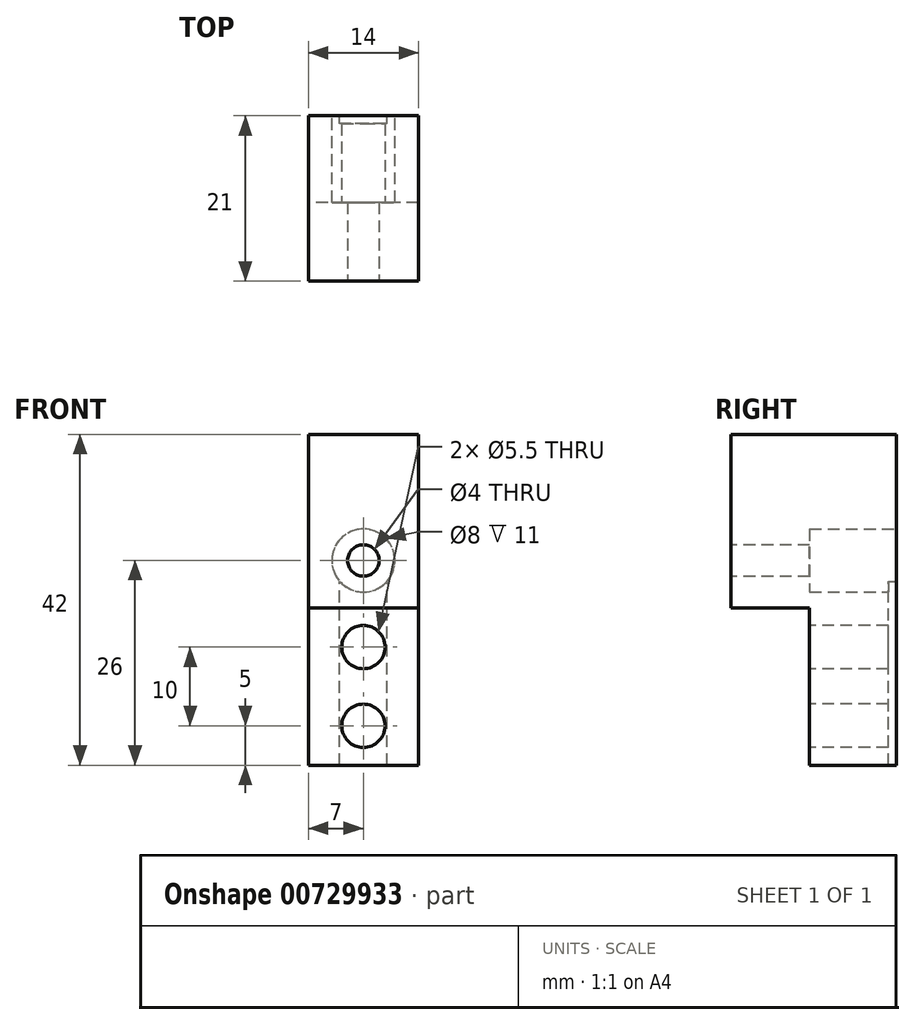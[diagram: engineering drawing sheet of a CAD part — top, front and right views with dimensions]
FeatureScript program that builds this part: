
annotation { "Feature Type Name" : "Feature", "Feature Type Description" : "" }
export const myFeature = defineFeature(function(context is Context, id is Id, definition is map)
    precondition{}
    {
        {
            var Q0;
            Q0=qCreatedBy(makeId("Front.planeOp"),FACE);
            var sketch = newSketch(context, id + "F0", { "sketchPlane" : qUnion([Q0])});
            skLineSegment(sketch, "E0.bottom", {"start": v(0, 0) * mm, "end": v(-14, 0) * mm});
            skLineSegment(sketch, "E0.top", {"start": v(0, 42) * mm, "end": v(-14, 42) * mm});
            skLineSegment(sketch, "E0.left", {"start": v(0, 0) * mm, "end": v(0, 42) * mm});
            skLineSegment(sketch, "E0.right", {"start": v(-14, 0) * mm, "end": v(-14, 42) * mm});
            skCircle(sketch, "E1", {"center": v(-7, 15) * mm, "radius": 2.75 * mm});
            skCircle(sketch, "E2", {"center": v(-7, 5) * mm, "radius": 2.75 * mm});
            skLineSegment(sketch, "E3", {"start": v(-14, 20) * mm, "end": v(0, 20) * mm});
            skCircle(sketch, "E4", {"center": v(-7, 26) * mm, "radius": 2 * mm});
            skSolve(sketch);
        }
        {
            var Q0;
            {var subQ1=sQuery(id+"F0.wireOp",EDGE,"E0.top");Q0=makeQuery(id+"F0.imprint","IMPRINT",FACE,{"disambiguationData":[TD([[makeQuery(id+"F0.imprint","IMPRINT",EDGE,{"derivedFrom":subQ1}),1.0]])]});}
            var Q1;
            {var subQ1=sQuery(id+"F0.wireOp",EDGE,"E0.bottom");Q1=makeQuery(id+"F0.imprint","IMPRINT",FACE,{"disambiguationData":[TD([[makeQuery(id+"F0.imprint","IMPRINT",EDGE,{"derivedFrom":subQ1}),-1.0]])]});}
            extrude(context, id + "F1", {"entities" : qUnion([Q0, Q1]), "oppositeDirection" : true, "depth" : 21 * mm, "offsetDistance" : 25 * mm});
        }
        {
            var Q0;
            {var subQ1=sQuery(id+"F0.wireOp",EDGE,"E0.bottom");Q0=makeQuery(id+"F0.imprint","IMPRINT",FACE,{"disambiguationData":[TD([[makeQuery(id+"F0.imprint","IMPRINT",EDGE,{"derivedFrom":subQ1}),-1.0]])]});}
            extrude(context, id + "F2", {"entities" : qUnion([Q0]), "operationType" : NewBodyOperationType.REMOVE, "oppositeDirection" : true, "depth" : 10 * mm, "offsetDistance" : 25 * mm});
        }
        {
            var Q0;
            Q0=makeQuery(id+"F1.opExtrude","CAP_FACE",FACE,{"disambiguationData":[OSD([sQuery(id+"F0.wireOp",EDGE,"E0.bottom"),sQuery(id+"F0.wireOp",EDGE,"E0.top"),sQuery(id+"F0.wireOp",EDGE,"E0.left"),sQuery(id+"F0.wireOp",EDGE,"E0.right"),sQuery(id+"F0.wireOp",EDGE,"E1"),sQuery(id+"F0.wireOp",EDGE,"E2"),sQuery(id+"F0.wireOp",EDGE,"E4")])],"isStart":false});
            var sketch = newSketch(context, id + "F3", { "sketchPlane" : qUnion([Q0])});
            skCircle(sketch, "E5", {"center": v(7, 26) * mm, "radius": 4 * mm});
            skSolve(sketch);
        }
        {
            var Q0;
            Q0=makeQuery(id+"F3.imprint","IMPRINT",FACE,{"disambiguationData":[TD([[makeQuery(id+"F3.imprint","IMPRINT",EDGE,{"derivedFrom":sQuery(id+"F3.wireOp",EDGE,"E5")}),1.0]])]});
            extrude(context, id + "F4", {"entities" : qUnion([Q0]), "operationType" : NewBodyOperationType.REMOVE, "oppositeDirection" : true, "depth" : 11 * mm, "offsetDistance" : 25 * mm});
        }
        {
            var Q0;
            Q0=makeQuery(id+"F1.opExtrude","CAP_FACE",FACE,{"disambiguationData":[OSD([sQuery(id+"F0.wireOp",EDGE,"E0.bottom"),sQuery(id+"F0.wireOp",EDGE,"E0.top"),sQuery(id+"F0.wireOp",EDGE,"E0.left"),sQuery(id+"F0.wireOp",EDGE,"E0.right"),sQuery(id+"F0.wireOp",EDGE,"E1"),sQuery(id+"F0.wireOp",EDGE,"E2"),sQuery(id+"F0.wireOp",EDGE,"E4")])],"isStart":false});
            var sketch = newSketch(context, id + "F5", { "sketchPlane" : qUnion([Q0])});
            skLineSegment(sketch, "E6", {"start": v(4, 0) * mm, "end": v(4, 23.35) * mm});
            skLineSegment(sketch, "E7", {"start": v(10, 0) * mm, "end": v(10, 23.35) * mm});
            skSolve(sketch);
        }
        {
            var Q0;
            {var subQ1=sQuery(id+"F5.wireOp",EDGE,"E6");Q0=makeQuery(id+"F5.imprint","IMPRINT",FACE,{"disambiguationData":[TD([[makeQuery(id+"F5.imprint","IMPRINT",EDGE,{"derivedFrom":subQ1}),-1.0]])]});}
            extrude(context, id + "F6", {"entities" : qUnion([Q0]), "operationType" : NewBodyOperationType.REMOVE, "oppositeDirection" : true, "depth" : 1 * mm, "offsetDistance" : 25 * mm});
        }
    });
